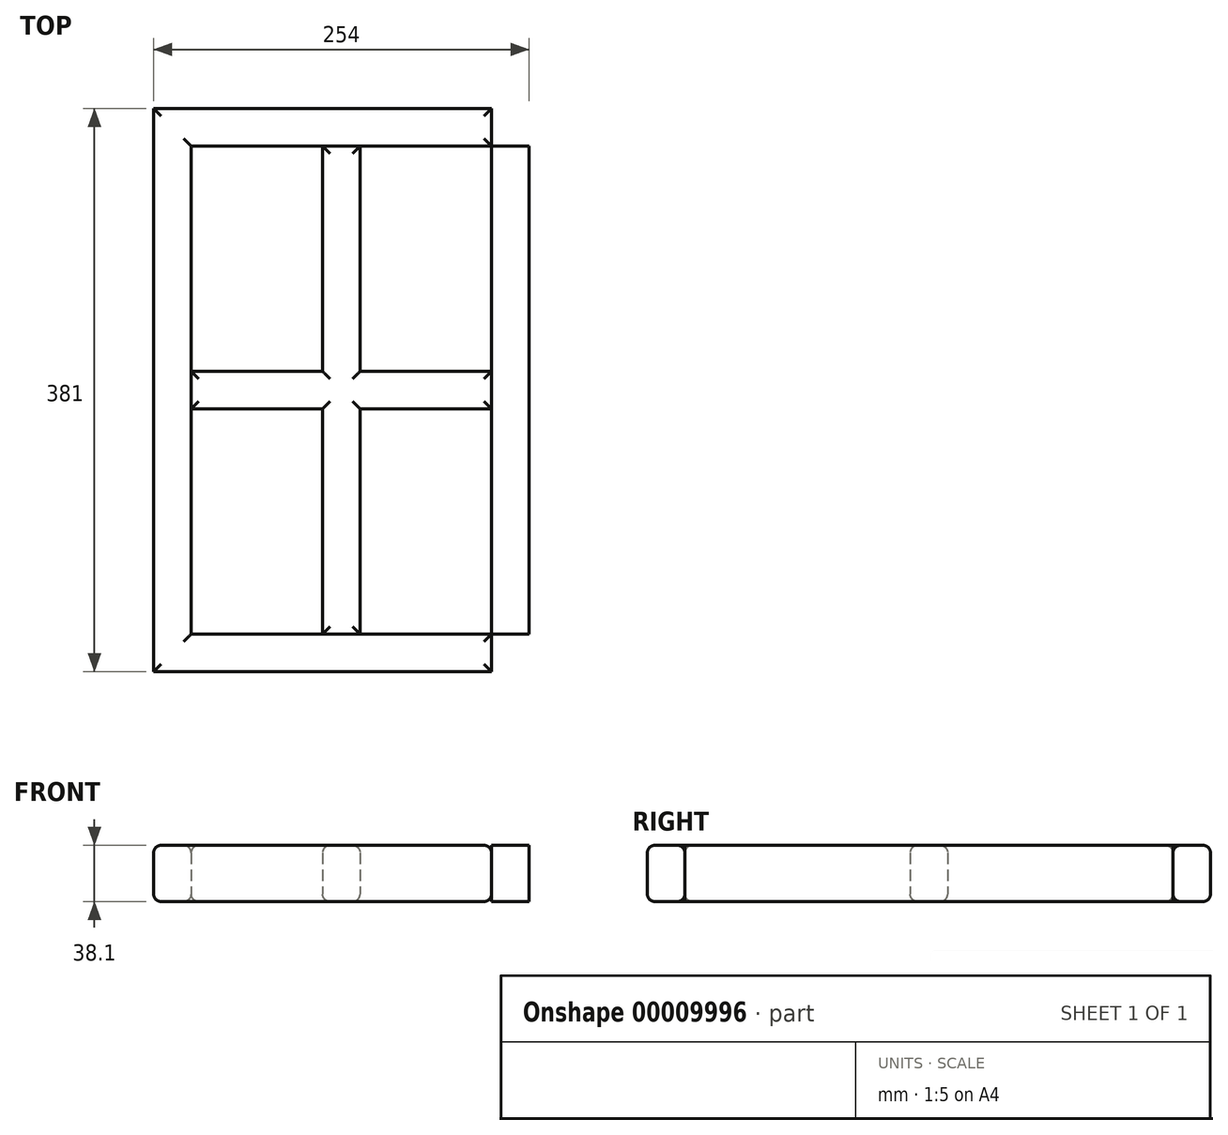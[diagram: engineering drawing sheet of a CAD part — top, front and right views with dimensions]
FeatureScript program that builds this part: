
annotation { "Feature Type Name" : "Feature", "Feature Type Description" : "" }
export const myFeature = defineFeature(function(context is Context, id is Id, definition is map)
    precondition{}
    {
        {
            var Q0;
            Q0=qCreatedBy(makeId("Top.planeOp"),FACE);
            var sketch = newSketch(context, id + "F0", { "sketchPlane" : qUnion([Q0])});
            skLineSegment(sketch, "E0.bottom", {"start": v(-64.39, 270.14) * mm, "end": v(-38.99, 270.14) * mm});
            skLineSegment(sketch, "E0.top", {"start": v(-64.39, -110.86) * mm, "end": v(-38.99, -110.86) * mm});
            skLineSegment(sketch, "E0.left", {"start": v(-64.39, 270.14) * mm, "end": v(-64.39, -110.86) * mm});
            skLineSegment(sketch, "E0.right", {"start": v(-38.99, 270.14) * mm, "end": v(-38.99, -110.86) * mm});
            skLineSegment(sketch, "E1.bottom", {"start": v(-64.39, -110.86) * mm, "end": v(189.61, -110.86) * mm});
            skLineSegment(sketch, "E1.top", {"start": v(-64.39, -85.46) * mm, "end": v(189.61, -85.46) * mm});
            skLineSegment(sketch, "E1.left", {"start": v(-64.39, -110.86) * mm, "end": v(-64.39, -85.46) * mm});
            skLineSegment(sketch, "E1.right", {"start": v(189.61, -110.86) * mm, "end": v(189.61, -85.46) * mm});
            skLineSegment(sketch, "E2.bottom", {"start": v(189.61, -110.86) * mm, "end": v(164.21, -110.86) * mm});
            skLineSegment(sketch, "E2.top", {"start": v(189.61, 270.14) * mm, "end": v(164.21, 270.14) * mm});
            skLineSegment(sketch, "E2.left", {"start": v(189.61, -110.86) * mm, "end": v(189.61, 270.14) * mm});
            skLineSegment(sketch, "E2.right", {"start": v(164.21, -110.86) * mm, "end": v(164.21, 270.14) * mm});
            skLineSegment(sketch, "E3.bottom", {"start": v(-64.39, 270.14) * mm, "end": v(189.61, 270.14) * mm});
            skLineSegment(sketch, "E3.top", {"start": v(-64.39, 244.74) * mm, "end": v(189.61, 244.74) * mm});
            skLineSegment(sketch, "E3.left", {"start": v(-64.39, 270.14) * mm, "end": v(-64.39, 244.74) * mm});
            skLineSegment(sketch, "E3.right", {"start": v(189.61, 270.14) * mm, "end": v(189.61, 244.74) * mm});
            skSolve(sketch);
        }
        {
            var Q0;
            {var subQ3=sQuery(id+"F0.wireOp",EDGE,"E0.right");var subQ5=sQuery(id+"F0.wireOp",EDGE,"E3.bottom");var subQ7=makeQuery(id+"F0.imprint","INTERSECT",VERTEX,{"derivedFrom":[subQ3,subQ5]});Q0=makeQuery(id+"F0.imprint","IMPRINT",FACE,{"disambiguationData":[TD([[makeQuery(id+"F0.imprint","IMPRINT",EDGE,{"disambiguationData":[TD([[subQ7,-1.0]])],"derivedFrom":subQ3}),1.0]])]});}
            var Q1;
            {var subQ0=sQuery(id+"F0.wireOp",EDGE,"E3.left");Q1=makeQuery(id+"F0.imprint","IMPRINT",FACE,{"disambiguationData":[TD([[makeQuery(id+"F0.imprint","IMPRINT",EDGE,{"derivedFrom":subQ0}),1.0]])]});}
            var Q2;
            {var subQ3=sQuery(id+"F0.wireOp",EDGE,"E0.left");Q2=makeQuery(id+"F0.imprint","IMPRINT",FACE,{"disambiguationData":[TD([[makeQuery(id+"F0.imprint","IMPRINT",EDGE,{"derivedFrom":subQ3}),1.0]])]});}
            var Q3;
            {var subQ3=sQuery(id+"F0.wireOp",EDGE,"E1.bottom");var subQ5=sQuery(id+"F0.wireOp",EDGE,"E0.right");var subQ7=makeQuery(id+"F0.imprint","INTERSECT",VERTEX,{"derivedFrom":[subQ5,subQ3]});Q3=makeQuery(id+"F0.imprint","IMPRINT",FACE,{"disambiguationData":[TD([[makeQuery(id+"F0.imprint","IMPRINT",EDGE,{"disambiguationData":[TD([[subQ7,1.0]])],"derivedFrom":subQ5}),1.0]])]});}
            var Q4;
            {var subQ0=sQuery(id+"F0.wireOp",EDGE,"E1.left");Q4=makeQuery(id+"F0.imprint","IMPRINT",FACE,{"disambiguationData":[TD([[makeQuery(id+"F0.imprint","IMPRINT",EDGE,{"derivedFrom":subQ0}),-1.0]])]});}
            var Q5;
            {var subQ3=sQuery(id+"F0.wireOp",EDGE,"E2.bottom");Q5=makeQuery(id+"F0.imprint","IMPRINT",FACE,{"disambiguationData":[TD([[makeQuery(id+"F0.imprint","IMPRINT",EDGE,{"derivedFrom":subQ3}),-1.0]])]});}
            var Q6;
            {var subQ3=sQuery(id+"F0.wireOp",EDGE,"E2.left");var subQ5=sQuery(id+"F0.wireOp",EDGE,"E1.top");var subQ7=makeQuery(id+"F0.imprint","INTERSECT",VERTEX,{"derivedFrom":[subQ5,subQ3]});Q6=makeQuery(id+"F0.imprint","IMPRINT",FACE,{"disambiguationData":[TD([[makeQuery(id+"F0.imprint","IMPRINT",EDGE,{"disambiguationData":[TD([[subQ7,1.0]])],"derivedFrom":subQ5}),1.0]])]});}
            var Q7;
            {var subQ0=sQuery(id+"F0.wireOp",EDGE,"E3.right");Q7=makeQuery(id+"F0.imprint","IMPRINT",FACE,{"disambiguationData":[TD([[makeQuery(id+"F0.imprint","IMPRINT",EDGE,{"derivedFrom":subQ0}),-1.0]])]});}
            extrude(context, id + "F1", {"entities" : qUnion([Q0, Q1, Q2, Q3, Q4, Q5, Q6, Q7]), "depth" : 38.1 * mm});
        }
        {
            var Q0;
            Q0=makeQuery(id+"F1.opExtrude","CAP_FACE",FACE,{"disambiguationData":[OSD([sQuery(id+"F0.wireOp",EDGE,"E0.left"),sQuery(id+"F0.wireOp",EDGE,"E0.right"),sQuery(id+"F0.wireOp",EDGE,"E1.bottom"),sQuery(id+"F0.wireOp",EDGE,"E1.top"),sQuery(id+"F0.wireOp",EDGE,"E1.left"),sQuery(id+"F0.wireOp",EDGE,"E2.bottom"),sQuery(id+"F0.wireOp",EDGE,"E2.left"),sQuery(id+"F0.wireOp",EDGE,"E2.right"),sQuery(id+"F0.wireOp",EDGE,"E3.bottom"),sQuery(id+"F0.wireOp",EDGE,"E3.top"),sQuery(id+"F0.wireOp",EDGE,"E3.left"),sQuery(id+"F0.wireOp",EDGE,"E3.right")])],"isStart":true});
            var sketch = newSketch(context, id + "F2", { "sketchPlane" : qUnion([Q0])});
            skLineSegment(sketch, "E4.bottom", {"start": v(49.91, 85.46) * mm, "end": v(75.31, 85.46) * mm});
            skLineSegment(sketch, "E4.top", {"start": v(49.91, -244.74) * mm, "end": v(75.31, -244.74) * mm});
            skLineSegment(sketch, "E4.left", {"start": v(49.91, 85.46) * mm, "end": v(49.91, -244.74) * mm});
            skLineSegment(sketch, "E4.right", {"start": v(75.31, 85.46) * mm, "end": v(75.31, -244.74) * mm});
            skLineSegment(sketch, "E5.bottom", {"start": v(-38.99, -66.94) * mm, "end": v(164.21, -66.94) * mm});
            skLineSegment(sketch, "E5.top", {"start": v(-38.99, -92.34) * mm, "end": v(164.21, -92.34) * mm});
            skLineSegment(sketch, "E5.left", {"start": v(-38.99, -66.94) * mm, "end": v(-38.99, -92.34) * mm});
            skLineSegment(sketch, "E5.right", {"start": v(164.21, -66.94) * mm, "end": v(164.21, -92.34) * mm});
            skSolve(sketch);
        }
        {
            var Q0;
            {var subQ6=sQuery(id+"F2.wireOp",EDGE,"E4.bottom");Q0=makeQuery(id+"F2.imprint","IMPRINT",FACE,{"disambiguationData":[TD([[makeQuery(id+"F2.imprint","IMPRINT",EDGE,{"derivedFrom":subQ6}),-1.0]])]});}
            var Q1;
            {var subQ0=sQuery(id+"F2.wireOp",EDGE,"E5.left");Q1=makeQuery(id+"F2.imprint","IMPRINT",FACE,{"disambiguationData":[TD([[makeQuery(id+"F2.imprint","IMPRINT",EDGE,{"derivedFrom":subQ0}),-1.0]])]});}
            var Q2;
            {var subQ3=sQuery(id+"F2.wireOp",EDGE,"E4.left");var subQ5=sQuery(id+"F2.wireOp",EDGE,"E5.bottom");var subQ7=makeQuery(id+"F2.imprint","INTERSECT",VERTEX,{"derivedFrom":[subQ3,subQ5]});Q2=makeQuery(id+"F2.imprint","IMPRINT",FACE,{"disambiguationData":[TD([[makeQuery(id+"F2.imprint","IMPRINT",EDGE,{"disambiguationData":[TD([[subQ7,-1.0]])],"derivedFrom":subQ3}),1.0]])]});}
            var Q3;
            {var subQ6=sQuery(id+"F2.wireOp",EDGE,"E4.top");Q3=makeQuery(id+"F2.imprint","IMPRINT",FACE,{"disambiguationData":[TD([[makeQuery(id+"F2.imprint","IMPRINT",EDGE,{"derivedFrom":subQ6}),1.0]])]});}
            var Q4;
            {var subQ0=sQuery(id+"F2.wireOp",EDGE,"E5.right");Q4=makeQuery(id+"F2.imprint","IMPRINT",FACE,{"disambiguationData":[TD([[makeQuery(id+"F2.imprint","IMPRINT",EDGE,{"derivedFrom":subQ0}),-1.0]])]});}
            extrude(context, id + "F3", {"entities" : qUnion([Q0, Q1, Q2, Q3, Q4]), "oppositeDirection" : true, "depth" : 38.1 * mm});
        }
        {
            var Q0;
            Q0=makeQuery(id+"F1.opExtrude","CAP_FACE",FACE,{"disambiguationData":[OSD([sQuery(id+"F0.wireOp",EDGE,"E0.left"),sQuery(id+"F0.wireOp",EDGE,"E0.right"),sQuery(id+"F0.wireOp",EDGE,"E1.bottom"),sQuery(id+"F0.wireOp",EDGE,"E1.top"),sQuery(id+"F0.wireOp",EDGE,"E1.left"),sQuery(id+"F0.wireOp",EDGE,"E2.bottom"),sQuery(id+"F0.wireOp",EDGE,"E2.left"),sQuery(id+"F0.wireOp",EDGE,"E2.right"),sQuery(id+"F0.wireOp",EDGE,"E3.bottom"),sQuery(id+"F0.wireOp",EDGE,"E3.top"),sQuery(id+"F0.wireOp",EDGE,"E3.left"),sQuery(id+"F0.wireOp",EDGE,"E3.right")])],"isStart":false});
            var Q1;
            Q1=makeQuery(id+"F3.opExtrude","CAP_FACE",FACE,{"disambiguationData":[OSD([sQuery(id+"F2.wireOp",EDGE,"E4.bottom"),sQuery(id+"F2.wireOp",EDGE,"E4.top"),sQuery(id+"F2.wireOp",EDGE,"E4.left"),sQuery(id+"F2.wireOp",EDGE,"E4.right"),sQuery(id+"F2.wireOp",EDGE,"E5.bottom"),sQuery(id+"F2.wireOp",EDGE,"E5.top"),sQuery(id+"F2.wireOp",EDGE,"E5.left"),sQuery(id+"F2.wireOp",EDGE,"E5.right")])],"isStart":false});
            var Q2;
            Q2=makeQuery(id+"F1.opExtrude","CAP_FACE",FACE,{"disambiguationData":[OSD([sQuery(id+"F0.wireOp",EDGE,"E0.left"),sQuery(id+"F0.wireOp",EDGE,"E0.right"),sQuery(id+"F0.wireOp",EDGE,"E1.bottom"),sQuery(id+"F0.wireOp",EDGE,"E1.top"),sQuery(id+"F0.wireOp",EDGE,"E1.left"),sQuery(id+"F0.wireOp",EDGE,"E2.bottom"),sQuery(id+"F0.wireOp",EDGE,"E2.left"),sQuery(id+"F0.wireOp",EDGE,"E2.right"),sQuery(id+"F0.wireOp",EDGE,"E3.bottom"),sQuery(id+"F0.wireOp",EDGE,"E3.top"),sQuery(id+"F0.wireOp",EDGE,"E3.left"),sQuery(id+"F0.wireOp",EDGE,"E3.right")])],"isStart":true});
            var Q3;
            Q3=makeQuery(id+"F3.opExtrude","CAP_FACE",FACE,{"disambiguationData":[OSD([sQuery(id+"F2.wireOp",EDGE,"E4.bottom"),sQuery(id+"F2.wireOp",EDGE,"E4.top"),sQuery(id+"F2.wireOp",EDGE,"E4.left"),sQuery(id+"F2.wireOp",EDGE,"E4.right"),sQuery(id+"F2.wireOp",EDGE,"E5.bottom"),sQuery(id+"F2.wireOp",EDGE,"E5.top"),sQuery(id+"F2.wireOp",EDGE,"E5.left"),sQuery(id+"F2.wireOp",EDGE,"E5.right")])],"isStart":true});
            fillet(context, id + "F4", {"entities" : qUnion([Q0, Q1, Q2, Q3]), "radius" : 5.08 * mm, "tangentPropagation" : true, "allowEdgeOverflow" : false});
        }
    });
